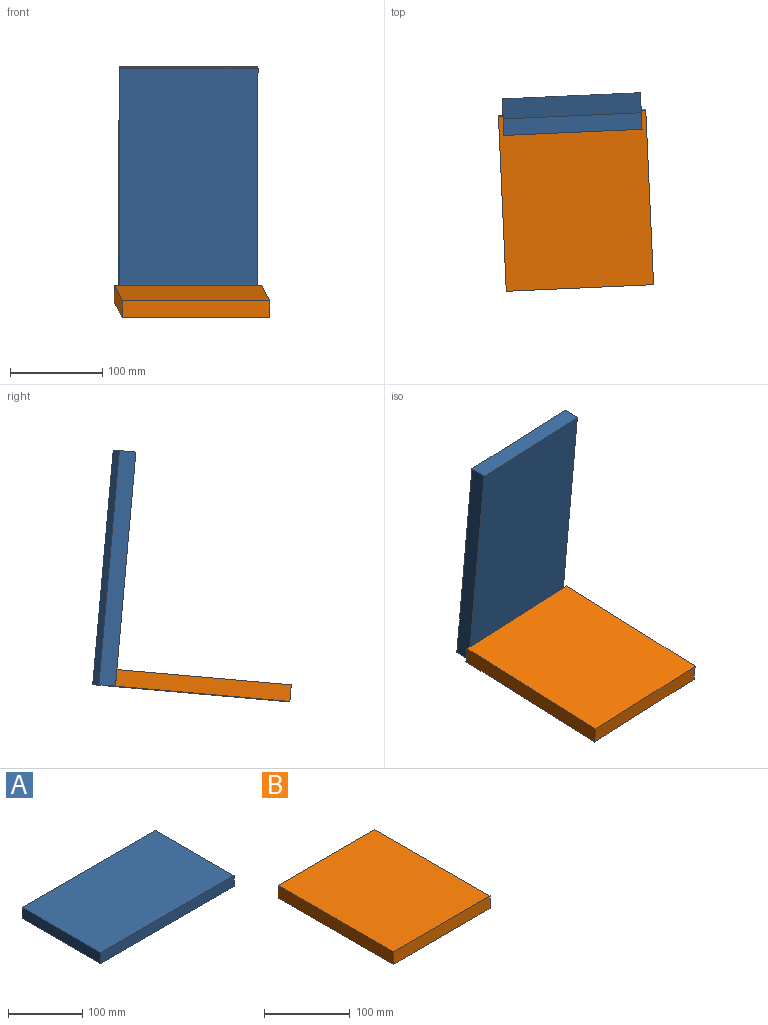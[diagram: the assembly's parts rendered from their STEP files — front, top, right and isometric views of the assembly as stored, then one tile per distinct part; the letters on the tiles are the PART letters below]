
ASSEMBLY  parts=2 mates=1
PART A: 6 faces, bbox 255x150x18 mm
  f0: plane 150x18mm, normal (-1,0,0), area 2700mm2, adj f1,f3,f4,f5
  f1: plane 255x18mm, normal (0,-1,0), area 4590mm2, adj f0,f2,f4,f5
  f2: plane 150x18mm, normal (1,0,0), area 2700mm2, adj f1,f3,f4,f5
  f3: plane 255x18mm, normal (0,1,0), area 4590mm2, adj f0,f2,f4,f5
  f4: plane 255x150mm, normal (0,0,1), area 38250mm2, adj f0,f1,f2,f3
  f5: plane 255x150mm, normal (0,0,-1), area 38250mm2, adj f0,f1,f2,f3
PART B: 6 faces, bbox 160x190x18 mm
  f0: plane 190x18mm, normal (-1,0,0), area 3420mm2, adj f1,f3,f4,f5
  f1: plane 160x18mm, normal (0,-1,0), area 2880mm2, adj f0,f2,f4,f5
  f2: plane 190x18mm, normal (1,0,0), area 3420mm2, adj f1,f3,f4,f5
  f3: plane 160x18mm, normal (0,1,0), area 2880mm2, adj f0,f2,f4,f5
  f4: plane 190x160mm, normal (0,0,1), area 30400mm2, adj f0,f1,f2,f3
  f5: plane 190x160mm, normal (0,0,-1), area 30400mm2, adj f0,f1,f2,f3
PLACE A rot(axis=(0.58,0.61,-0.54),121.5deg) t=(145.13,193.02,282.08)mm
PLACE B rot(axis=(0.89,0.02,0.46),5.6deg) t=(148.42,7.99,9.93)mm
MATE fastened A.f4 <-> B.f3  axis (0.04,-1,-0.09) through (219.86,200.66,26.49)mm
